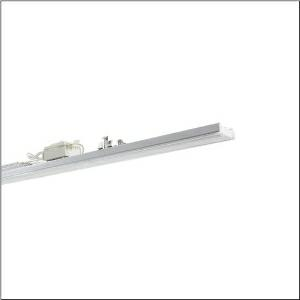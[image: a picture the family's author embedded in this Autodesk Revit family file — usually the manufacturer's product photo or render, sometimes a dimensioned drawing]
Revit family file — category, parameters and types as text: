
# Revit family: licross_21_recessed_ho_52tl12dv4l2m3s4
name_source: partatom
category: Lighting Fixtures
units: mm (PartAtom-declared; Revit-internal decimal feet)

## family parameters
Cut with Voids When Loaded = No
Host = Face
Light Source = No
Part Type = Normal
Room Calculation Point = No
Round Connector Dimension = Use Diameter
Shared = No

## types (1)
- --- (1 x LED, 910 lm, 6.4 W, 4000K)
    Apparent Load = 6 VA
    CIE Flux Codes = 69 91 98 100 100
    Color Rendering = 80
    Color Temperature = 4000K
    Default Elevation = 1800 mm
    Description = Licross 21 Recessed HO, luminaire insert, of sheet steel, galvanised, coil coated, white, length: 2.250mm, width: 66mm, height: 67mm, LED rated luminous flux: 22.710lm, light colour: 840, SDCM (Standard Deviation of Colour Matching)MacAdam ≤ 3 SDCM (initial), control gear: DALI 2, with plug, 6-pole, with phase selection, for trunking rail, 9 or 11-core, mains connection: 220..240V, AC, 50/60Hz, rated input power: 129W, for trunking rail, 9-/11-core, internal wiring halogen-free, for emergency light function, converter,control gear: single battery element, battery: LiFePO4, 9Ah, primary optical cover: cover, of PMMA, light emission: direct distribution, primary light characteristic: symmetric, protection rating (complete): IP40, insulation class (complete): insulation class I (protective earthing), certification: CE, UKCA, protection symbol: D if used in an environment without relevant dust loads with corresponding accessories, impact resistance: IK06, permissible ambient temperature for indoor applications: +5..+30°C, standard: EN 60598-2-22, LABS conformity tested according to VDMA 24364:2018-05, reducing of maximum allowable ambient temperature of 5°C with ceiling mounting, corresponds to IFS (International Featured Standards) requirements for safety and quality in the food industry, The light source and the operating device comply with the requirements of the Ecodesign Regulation (EU) 2019/2020 and are replaceable in accordance with this regulation, packaging unit: 1 piece
    Height = 58 mm
    Lamp = 1 x LED
    Lamp Light Flux = 910 lm
    Lamp Power = 6.4 W
    Lamp count = 1
    Length = 2250 mm
    Luminous efficacy = 142 lm/W
    Manufacturer = Siteco
    ModVariant = No
    Model = 52TL12DV4L2M3S4
    Mounting Place = Ceiling
    Mounting Type = Pendant
    Number of Poles = 1
    OnlyDefault = Yes
    Power Factor = 1
    Product Name = Licross 21 Recessed HO
    Product group = luminaire insert | ceiling pendant
    ProductGroupID = 901
    Protection Class = Protection class I
    Protection Degree = IP 40
    RLX_Detail_Level = 1
    RLX_Emergency_Light_Flux = 0 lm
    RLX_Emergency_Type = 0
    RLX_Emergency_Type_DB = No
    RlxData = <blob elided: 30125 chars, md5=3a1a933b>
    Socket = socket
    Standby Power = 0 W
    System Light Flux = 910 lm
    System Power = 6 W
    Type Comments = : emergency light operation: 3 h
    Type Image = l_1296930.jpg
    URL = http://relux.com
    VarID = @adj_109231
    Voltage = 0 V
    Weight = 0.00 kg
    Width = 66 mm

## geometry (parser evidence)
native form markers: Blend x4, Sweep x11
no freeform markers — native parametric forms only
